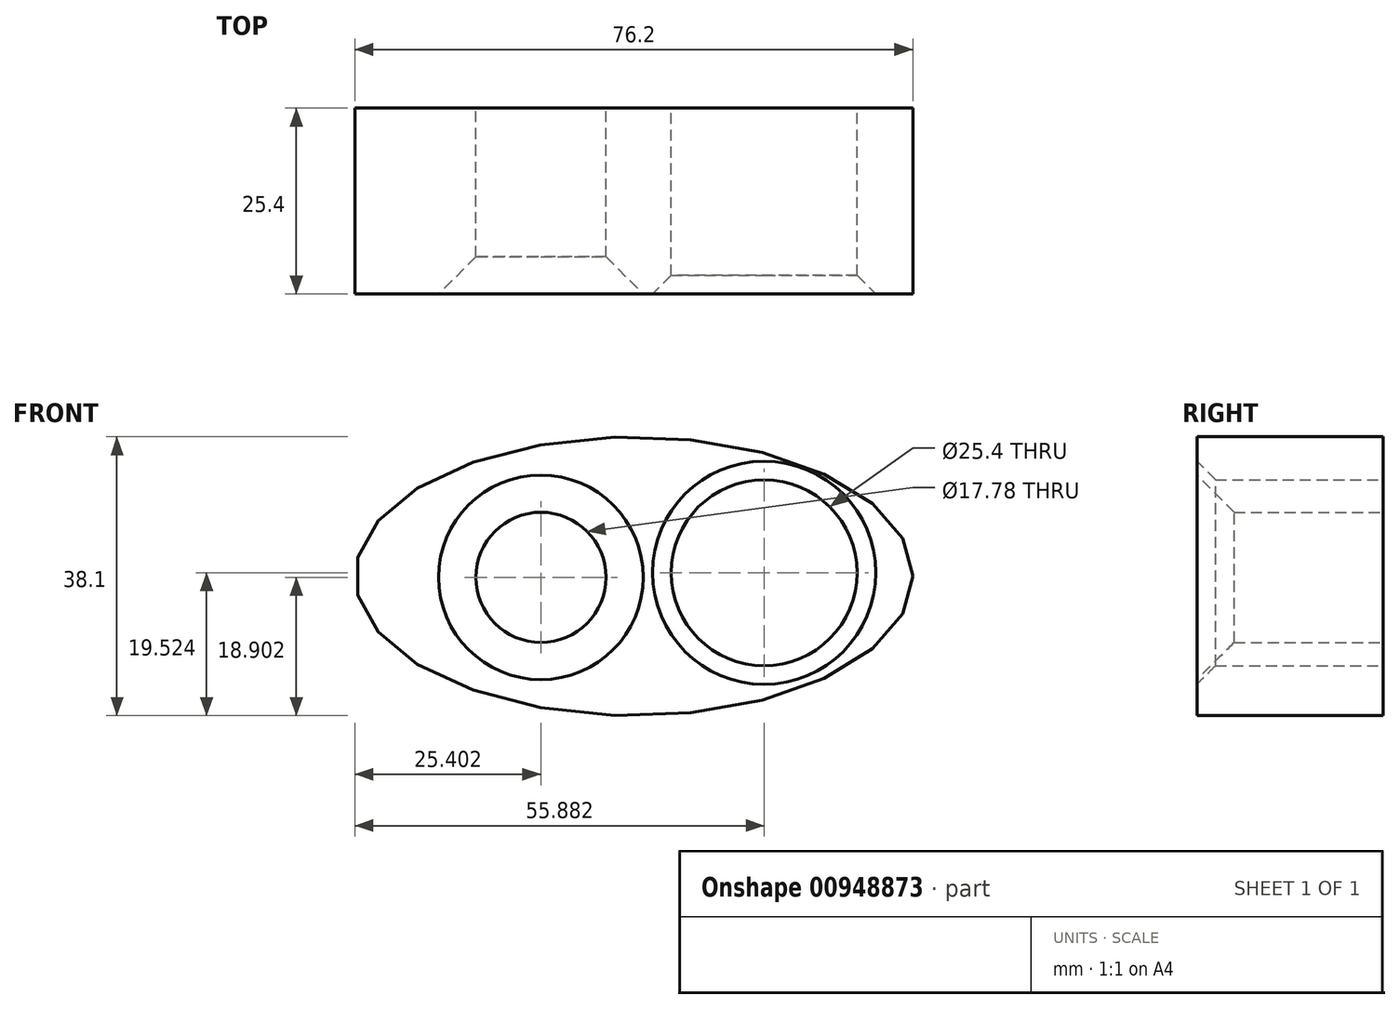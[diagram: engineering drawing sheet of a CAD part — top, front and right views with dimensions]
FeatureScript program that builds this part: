
annotation { "Feature Type Name" : "Feature", "Feature Type Description" : "" }
export const myFeature = defineFeature(function(context is Context, id is Id, definition is map)
    precondition{}
    {
        {
            var Q0;
            Q0=qCreatedBy(makeId("Front.planeOp"),FACE);
            var sketch = newSketch(context, id + "F0", { "sketchPlane" : qUnion([Q0])});
            skCircle(sketch, "E0", {"center": v(-27.3, 19.58) * mm, "radius": 8.9 * mm});
            skCircle(sketch, "E1", {"center": v(3.17, 20.2) * mm, "radius": 12.7 * mm});
            skEllipse(sketch, "E2", {"center": v(-14.6, 19.73) * mm, "majorRadius": 38.1 * mm, "minorRadius": 19.05 * mm, "majorAxis": v(1, 0)});
            skSolve(sketch);
        }
        {
            var Q0;
            Q0=makeQuery(id+"F0.imprint","IMPRINT",FACE,{"disambiguationData":[TD([[makeQuery(id+"F0.imprint","IMPRINT",EDGE,{"derivedFrom":sQuery(id+"F0.wireOp",EDGE,"E0")}),-1.0]])]});
            extrude(context, id + "F1", {"entities" : qUnion([Q0]), "depth" : 25.4 * mm, "offsetDistance" : 25.4 * mm});
        }
        {
            var Q0;
            Q0=makeQuery(id+"F1.opExtrude","CAP_EDGE",EDGE,{"disambiguationData":[OSD([sQuery(id+"F0.wireOp",EDGE,"E1")])],"isStart":false});
            chamfer(context, id + "F2", {"entities" : qUnion([Q0]), "width" : 2.54 * mm, "tangentPropagation" : true});
        }
        {
            var Q0;
            Q0=makeQuery(id+"F1.opExtrude","CAP_EDGE",EDGE,{"disambiguationData":[OSD([sQuery(id+"F0.wireOp",EDGE,"E0")])],"isStart":false});
            chamfer(context, id + "F3", {"entities" : qUnion([Q0]), "width" : 5.08 * mm, "tangentPropagation" : true});
        }
    });
